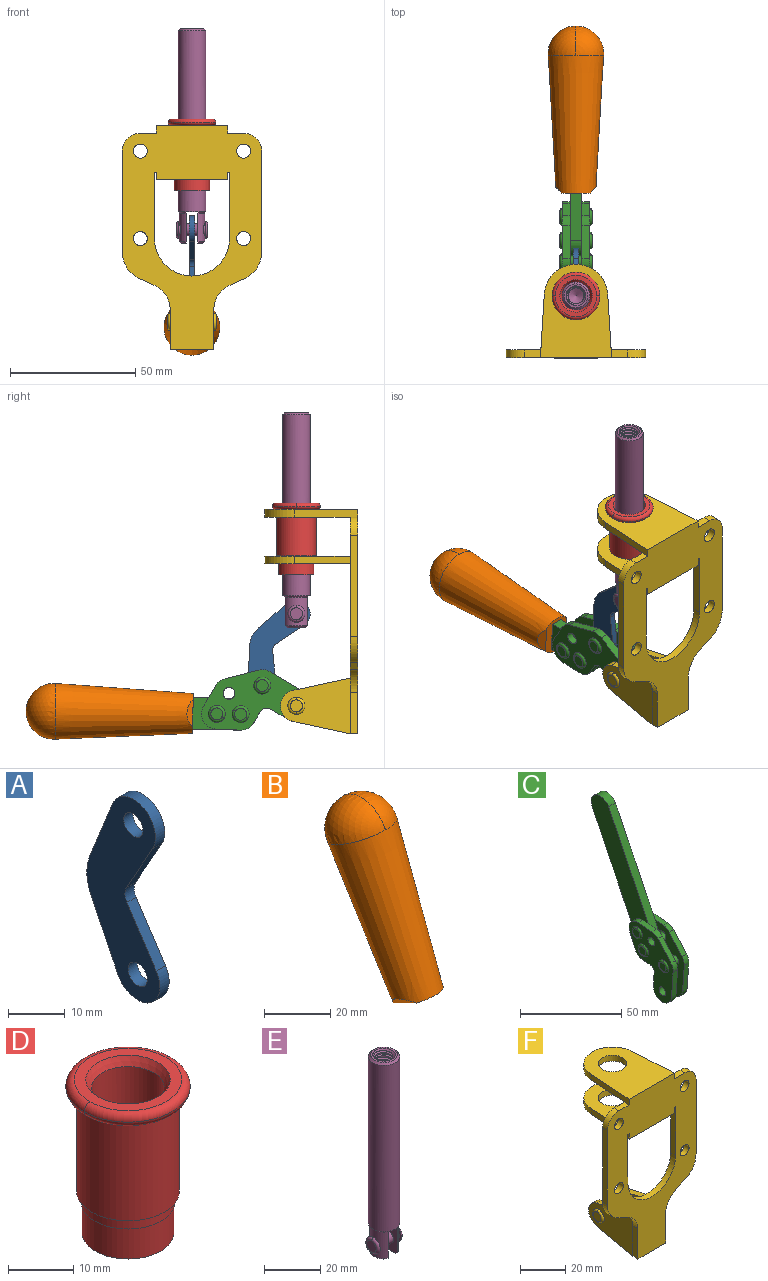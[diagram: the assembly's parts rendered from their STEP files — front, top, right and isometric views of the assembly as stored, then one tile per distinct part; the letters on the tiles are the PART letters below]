
ASSEMBLY  parts=6 mates=6
PART A: 12 faces, bbox 2.3x18.2x42.8 mm
  f0: cylinder r=2.4mm len=4.8mm, axis (1,0,0), area 34.9mm2, adj f4,f11
  f1: cylinder r=10.41mm len=8.47mm, axis (1,0,0), area 20.2mm2, adj f4,f9,f10,f11
  f2: cylinder r=3.05mm len=3.16mm, axis (1,0,0), area 7.7mm2, adj f4,f6,f7,f11
  f3: cylinder r=2.4mm len=4.8mm, axis (1,0,0), area 34.9mm2, adj f4,f11
  f4: plane 42.81x18.23mm, normal (-1,0,0), area 414.1mm2, adj f0,f1,f2,f3,f5,f6,f7,f8
  f5: cylinder r=5.54mm len=10.67mm, axis (1,0,0), area 41.8mm2, adj f4,f6,f10,f11
  f6: plane 11.66x6.53mm, normal (0,-0.87,-0.49), area 30.9mm2, adj f2,f4,f5,f11
  f7: plane 11.17x7.33mm, normal (0,-0.84,0.55), area 30.9mm2, adj f2,f4,f8,f11
  f8: cylinder r=5.54mm len=10.51mm, axis (1,0,0), area 41.8mm2, adj f4,f7,f9,f11
  f9: plane 13.67x6.67mm, normal (0,0.9,-0.44), area 35.1mm2, adj f1,f4,f8,f11
  f10: plane 14.1x5.7mm, normal (0,0.93,0.37), area 35.1mm2, adj f1,f4,f5,f11
  f11: plane 42.81x18.23mm, normal (1,0,0), area 414.1mm2, adj f0,f1,f2,f3,f5,f6,f7,f8
PART B: 11 faces, bbox 22.3x42.6x64.5 mm
  f0: sphere r=11.13mm, area 411.4mm2, adj f1,f8
  f1: cone r=11.11mm half-angle=3.3deg, axis (0,0.44,0.9), area 3251.8mm2, adj f0,f7,f8,f9,f10
  f2: cylinder r=6.16mm len=11.7mm, axis (1,0,0), area 89.5mm2, adj f3,f4,f5,f6
  f3: plane 60.23x36.75mm, normal (-1,0,0), area 763.6mm2, adj f2,f4,f6,f10
  f4: plane 51.37x25.05mm, normal (0,0.9,-0.44), area 264.2mm2, adj f2,f3,f5,f10
  f5: plane 60.23x36.75mm, normal (1,0,0), area 763.6mm2, adj f2,f4,f6,f10
  f6: plane 51.37x25.05mm, normal (0,-0.9,0.44), area 264.2mm2, adj f2,f3,f5,f10
  f7: plane 9.95x5.95mm, normal (0.71,-0.31,-0.64), area 25.8mm2, adj f1,f10
  f8: sphere r=11.13mm, area 411.4mm2, adj f0,f1
  f9: plane 9.95x5.95mm, normal (-0.71,-0.31,-0.64), area 25.8mm2, adj f1,f10
  f10: plane 14.27x11.38mm, normal (0,-0.44,-0.9), area 106.7mm2, adj f1,f3,f4,f5,f6,f7,f9
PART C: 59 faces, bbox 12.9x60.2x99.6 mm
  f0: torus R=2.39mm, axis (-1,0,0), area 14.9mm2, adj f20,f43,f51
  f1: torus R=2.39mm, axis (-1,0,0), area 14.9mm2, adj f19,f42,f51
  f2: torus R=2.39mm, axis (-1,0,0), area 14.9mm2, adj f18,f35,f51
  f3: torus R=2.39mm, axis (-1,0,0), area 14.9mm2, adj f14,f17,f23
  f4: torus R=2.39mm, axis (-1,0,0), area 14.9mm2, adj f13,f16,f23
  f5: torus R=2.39mm, axis (-1,0,0), area 14.9mm2, adj f12,f15,f23
  f6: cylinder r=2.39mm len=4.78mm, axis (1,0,0), area 46.5mm2, adj f48,f50,f51
  f7: cylinder r=2.39mm len=4.78mm, axis (1,0,0), area 46.5mm2, adj f50,f51
  f8: cylinder r=6.35mm len=12.68mm, axis (1,0,0), area 61.8mm2, adj f38,f39,f50,f51
  f9: cylinder r=2.39mm len=4.78mm, axis (-1,0,0), area 70.5mm2, adj f46,f50
  f10: cylinder r=2.39mm len=4.78mm, axis (-1,0,0), area 46.5mm2, adj f23,f45,f46
  f11: cylinder r=2.39mm len=4.78mm, axis (-1,0,0), area 46.5mm2, adj f23,f46
  f12: plane 4.78x4.78mm, normal (1,0,0), area 17.9mm2, adj f5,f15
  f13: plane 4.78x4.78mm, normal (1,0,0), area 17.9mm2, adj f4,f16
  f14: plane 4.78x4.78mm, normal (1,0,0), area 17.9mm2, adj f3,f17
  f15: torus R=2.39mm, axis (-1,0,0), area 14.9mm2, adj f5,f12,f23
  f16: torus R=2.39mm, axis (-1,0,0), area 14.9mm2, adj f4,f13,f23
  f17: torus R=2.39mm, axis (-1,0,0), area 14.9mm2, adj f3,f14,f23
  f18: plane 4.78x4.78mm, normal (-1,0,0), area 17.9mm2, adj f2,f35
  f19: plane 4.78x4.78mm, normal (-1,0,0), area 17.9mm2, adj f1,f42
  f20: plane 4.78x4.78mm, normal (-1,0,0), area 17.9mm2, adj f0,f43
  f21: plane 2.26x0.2mm, normal (1,0,0), area 0.2mm2, adj f31,f44
  f22: plane 2.26x0.2mm, normal (-1,0,0), area 0.2mm2, adj f41,f44
  f23: plane 39.37x30.77mm, normal (1,0,0), area 565.5mm2, adj f3,f4,f5,f10,f11,f15,f16,f17
  f24: cylinder r=6.1mm len=4.15mm, axis (-1,0,0), area 14.7mm2, adj f23,f25,f32,f46
  f25: plane 10.25x9.01mm, normal (0,-0.75,0.66), area 42.3mm2, adj f23,f24,f26,f46
  f26: cylinder r=6.35mm len=4.64mm, axis (-1,0,0), area 15.6mm2, adj f23,f25,f27,f46
  f27: plane 15.84x3.1mm, normal (0,-1,-0.07), area 49.2mm2, adj f23,f26,f28,f46
  f28: cylinder r=6.35mm len=12.68mm, axis (-1,0,0), area 61.8mm2, adj f23,f27,f29,f46
  f29: plane 8.11x3.1mm, normal (0,1,0.07), area 25.2mm2, adj f23,f28,f30,f46
  f30: cylinder r=3.05mm len=3.25mm, axis (-1,0,0), area 14.8mm2, adj f23,f29,f31,f46
  f31: plane 5.99x3.1mm, normal (0,0.07,-1), area 18.6mm2, adj f21,f23,f30,f44,f46
  f32: plane 9.5x3.1mm, normal (0,-0.07,1), area 29.5mm2, adj f23,f24,f33,f46,f47
  f33: cylinder r=6.1mm len=8.63mm, axis (-1,0,0), area 39.1mm2, adj f23,f32,f34,f47
  f34: plane 8.65x3.96mm, normal (0,0.91,-0.42), area 29.5mm2, adj f23,f33,f44,f47
  f35: torus R=2.39mm, axis (-1,0,0), area 14.9mm2, adj f2,f18,f51
  f36: plane 10.25x9.01mm, normal (0,-0.75,0.66), area 42.3mm2, adj f37,f49,f50,f51
  f37: cylinder r=6.35mm len=4.64mm, axis (1,0,0), area 15.6mm2, adj f36,f38,f50,f51
  f38: plane 15.84x3.1mm, normal (0,-1,-0.07), area 49.2mm2, adj f8,f37,f50,f51
  f39: plane 8.11x3.1mm, normal (0,1,0.07), area 25.2mm2, adj f8,f40,f50,f51
  f40: cylinder r=3.05mm len=3.25mm, axis (1,0,0), area 14.8mm2, adj f39,f41,f50,f51
  f41: plane 5.99x3.1mm, normal (0,0.07,-1), area 18.6mm2, adj f22,f40,f44,f50,f51
  f42: torus R=2.39mm, axis (-1,0,0), area 14.9mm2, adj f1,f19,f51
  f43: torus R=2.39mm, axis (-1,0,0), area 14.9mm2, adj f0,f20,f51
  f44: cylinder r=6.35mm len=12.12mm, axis (-1,0,0), area 128.9mm2, adj f21,f22,f23,f31,f34,f41,f46,f47
  f45: plane 2.65x1.35mm, normal (1,0,0), area 1mm2, adj f10,f55
  f46: plane 39.08x20.42mm, normal (-1,0,0), area 412.5mm2, adj f9,f10,f11,f24,f25,f26,f27,f28
  f47: plane 77.62x39.82mm, normal (1,0,0), area 850mm2, adj f32,f33,f34,f44,f53,f54,f55
  f48: plane 2.65x1.35mm, normal (-1,0,0), area 1mm2, adj f6,f55
  f49: cylinder r=6.1mm len=4.15mm, axis (1,0,0), area 14.7mm2, adj f36,f50,f51,f56
  f50: plane 39.08x20.42mm, normal (1,0,0), area 412.5mm2, adj f6,f7,f8,f9,f36,f37,f38,f39
  f51: plane 39.37x30.77mm, normal (-1,0,0), area 565.5mm2, adj f0,f1,f2,f6,f7,f8,f35,f36
  f52: plane 8.65x3.96mm, normal (0,0.91,-0.42), area 29.5mm2, adj f44,f51,f57,f58
  f53: plane 68.49x33.4mm, normal (0,0.9,-0.44), area 358.1mm2, adj f44,f47,f54,f58
  f54: cylinder r=6.35mm len=12.06mm, axis (1,0,0), area 93.7mm2, adj f47,f53,f55,f58
  f55: plane 68.49x33.4mm, normal (0,-0.9,0.44), area 358.1mm2, adj f44,f45,f46,f47,f48,f50,f54,f58
  f56: plane 9.5x3.1mm, normal (0,-0.07,1), area 29.5mm2, adj f49,f50,f51,f57,f58
  f57: cylinder r=6.1mm len=8.63mm, axis (1,0,0), area 39.1mm2, adj f51,f52,f56,f58
  f58: plane 77.62x39.82mm, normal (-1,0,0), area 850mm2, adj f44,f52,f53,f54,f55,f56,f57
PART D: 15 faces, bbox 20.6x20.6x28.7 mm
  f0: torus R=8.26mm, axis (0,0,1), area 56.8mm2, adj f1,f10,f12
  f1: torus R=8.26mm, axis (0,0,1), area 56.8mm2, adj f0,f6,f13
  f2: cylinder r=5.59mm len=25.91mm, axis (0,0,1), area 909.6mm2, adj f3,f4
  f3: cone r=6.86mm half-angle=45deg, axis (0,0,-1), area 70.2mm2, adj f2,f14
  f4: cone r=6.47mm half-angle=30deg, axis (0,0,1), area 66.7mm2, adj f2,f13
  f5: cylinder r=7.04mm len=14.07mm, axis (0,0,1), area 252.6mm2, adj f11,f14
  f6: torus R=8.26mm, axis (0,0,1), area 56.8mm2, adj f1,f12,f13
  f7: cylinder r=7.16mm len=14.33mm, axis (0,0,1), area 91.5mm2, adj f9,f11
  f8: cylinder r=7.86mm len=18.42mm, axis (0,0,1), area 909.6mm2, adj f9,f10
  f9: plane 15.72x15.72mm, normal (0,0,-1), area 33mm2, adj f7,f8
  f10: plane 16.51x16.51mm, normal (0,0,-1), area 19.9mm2, adj f0,f8,f12
  f11: plane 14.33x14.33mm, normal (0,0,-1), area 5.7mm2, adj f5,f7
  f12: torus R=8.26mm, axis (0,0,1), area 56.8mm2, adj f0,f6,f10
  f13: plane 16.51x16.51mm, normal (0,0,1), area 82.7mm2, adj f1,f4,f6
  f14: plane 14.07x14.07mm, normal (0,0,-1), area 7.8mm2, adj f3,f5
PART E: 48 faces, bbox 12.6x11.1x86.1 mm
  f0: torus R=2.41mm, axis (-1,0,0), area 15mm2, adj f30,f32,f34
  f1: torus R=2.41mm, axis (-1,0,0), area 15mm2, adj f29,f31,f33
  f2: cylinder r=5.54mm len=72.39mm, axis (0,0,1), area 2518.5mm2, adj f3,f4,f42,f43
  f3: cone r=5.54mm half-angle=45deg, axis (0,0,1), area 7.6mm2, adj f2,f5,f41
  f4: cone r=5.54mm half-angle=45deg, axis (0,0,-1), area 34.9mm2, adj f2,f39
  f5: cylinder r=5.08mm len=11.48mm, axis (0,0,1), area 108.3mm2, adj f3,f7,f8,f41
  f6: cylinder r=2.41mm len=4.83mm, axis (-1,0,0), area 71.2mm2, adj f40,f41
  f7: cylinder r=2.41mm len=4.83mm, axis (-1,0,0), area 7.6mm2, adj f5,f34
  f8: cone r=5.08mm half-angle=45deg, axis (0,0,1), area 10.6mm2, adj f5,f37,f41
  f9: cone r=3.98mm half-angle=45deg, axis (0,0,1), area 17.6mm2, adj f27,f39,f45,f46,f47
  f10: cylinder r=2.41mm len=4.83mm, axis (-1,0,0), area 7.6mm2, adj f33,f38
  f11: cylinder r=3.2mm len=6.4mm, axis (0,0,1), area 78.4mm2, adj f12,f28,f44,f45,f47
  f12: cylinder r=3.2mm len=6.4mm, axis (0,0,1), area 10.5mm2, adj f11,f13,f45,f47
  f13: cylinder r=3.2mm len=6.4mm, axis (0,0,1), area 10.5mm2, adj f12,f14,f45,f47
  f14: cylinder r=3.2mm len=6.4mm, axis (0,0,1), area 10.5mm2, adj f13,f15,f45,f47
  f15: cylinder r=3.2mm len=6.4mm, axis (0,0,1), area 10.5mm2, adj f14,f16,f45,f47
  f16: cylinder r=3.2mm len=6.4mm, axis (0,0,1), area 10.5mm2, adj f15,f17,f45,f47
  f17: cylinder r=3.2mm len=6.4mm, axis (0,0,1), area 10.5mm2, adj f16,f18,f45,f47
  f18: cylinder r=3.2mm len=6.4mm, axis (0,0,1), area 10.5mm2, adj f17,f19,f45,f47
  f19: cylinder r=3.2mm len=6.4mm, axis (0,0,1), area 10.5mm2, adj f18,f20,f45,f47
  f20: cylinder r=3.2mm len=6.4mm, axis (0,0,1), area 10.5mm2, adj f19,f21,f45,f47
  f21: cylinder r=3.2mm len=6.4mm, axis (0,0,1), area 10.5mm2, adj f20,f22,f45,f47
  f22: cylinder r=3.2mm len=6.4mm, axis (0,0,1), area 10.5mm2, adj f21,f23,f45,f47
  f23: cylinder r=3.2mm len=6.4mm, axis (0,0,1), area 10.5mm2, adj f22,f24,f45,f47
  f24: cylinder r=3.2mm len=6.4mm, axis (0,0,1), area 10.5mm2, adj f23,f25,f45,f47
  f25: cylinder r=3.2mm len=6.4mm, axis (0,0,1), area 10.5mm2, adj f24,f26,f45,f47
  f26: cylinder r=3.2mm len=6.4mm, axis (0,0,1), area 10.5mm2, adj f25,f27,f45,f47
  f27: cylinder r=3.2mm len=6.4mm, axis (0,0,1), area 7.4mm2, adj f9,f26,f45,f47
  f28: cone r=3.2mm half-angle=60deg, axis (0,0,1), area 37.2mm2, adj f11
  f29: plane 4.83x4.83mm, normal (-1,0,0), area 18.3mm2, adj f1,f31
  f30: plane 4.83x4.83mm, normal (1,0,0), area 18.3mm2, adj f0,f32
  f31: torus R=2.41mm, axis (-1,0,0), area 15mm2, adj f1,f29,f33
  f32: torus R=2.41mm, axis (-1,0,0), area 15mm2, adj f0,f30,f34
  f33: plane 6.83x6.83mm, normal (1,0,0), area 18.3mm2, adj f1,f10,f31
  f34: plane 6.83x6.83mm, normal (-1,0,0), area 18.3mm2, adj f0,f7,f32
  f35: cone r=5.08mm half-angle=45deg, axis (0,0,1), area 10.6mm2, adj f36,f38,f40
  f36: plane 7.25x1.97mm, normal (0,0,-1), area 10mm2, adj f35,f40
  f37: plane 7.25x1.97mm, normal (0,0,-1), area 10mm2, adj f8,f41
  f38: cylinder r=5.08mm len=11.48mm, axis (0,0,1), area 108.3mm2, adj f10,f35,f40,f42
  f39: plane 9.55x9.55mm, normal (0,0,1), area 22mm2, adj f4,f9
  f40: plane 12.76x10.09mm, normal (1,0,0), area 95.7mm2, adj f6,f35,f36,f38,f42,f43
  f41: plane 12.76x10.09mm, normal (-1,0,0), area 95.7mm2, adj f3,f5,f6,f8,f37,f43
  f42: cone r=5.54mm half-angle=45deg, axis (0,0,1), area 7.6mm2, adj f2,f38,f40
  f43: plane 11.07x4.7mm, normal (0,0,-1), area 50.4mm2, adj f2,f40,f41
  f44: plane 0.89x0.62mm, normal (-1,0,0), area 0.3mm2, adj f11,f45,f46,f47
  f45: bspline ~24.8x7.63mm, area 266.6mm2, adj f9,f11,f12,f13,f14,f15,f16,f17
  f46: bspline ~24.87x7.63mm, area 73.6mm2, adj f9,f44,f45,f47
  f47: bspline ~24.98x7.63mm, area 272.5mm2, adj f9,f11,f12,f13,f14,f15,f16,f17
PART F: 55 faces, bbox 55.7x37.4x89.8 mm
  f0: torus R=2.41mm, axis (-1,0,0), area 15mm2, adj f11,f15,f25
  f1: torus R=2.41mm, axis (-1,0,0), area 15mm2, adj f10,f12,f22
  f2: cylinder r=2.78mm len=5.56mm, axis (0,-1,0), area 54.2mm2, adj f30,f54
  f3: cylinder r=14.99mm len=29.97mm, axis (0,-1,0), area 145.9mm2, adj f30,f49,f53,f54
  f4: cylinder r=2.78mm len=5.56mm, axis (0,-1,0), area 54.2mm2, adj f30,f54
  f5: cylinder r=2.78mm len=5.56mm, axis (0,-1,0), area 54.2mm2, adj f30,f54
  f6: cylinder r=2.78mm len=5.56mm, axis (0,-1,0), area 54.2mm2, adj f30,f54
  f7: cylinder r=6.35mm len=12.7mm, axis (0,0,1), area 123.6mm2, adj f27,f51
  f8: cylinder r=6.35mm len=12.7mm, axis (0,0,-1), area 124.7mm2, adj f21,f35
  f9: cylinder r=2.41mm len=11.18mm, axis (-1,0,0), area 169.4mm2, adj f16,f19
  f10: plane 4.83x4.83mm, normal (1,0,0), area 18.3mm2, adj f1,f12
  f11: plane 4.83x4.83mm, normal (-1,0,0), area 18.3mm2, adj f0,f15
  f12: torus R=2.41mm, axis (-1,0,0), area 15mm2, adj f1,f10,f22
  f13: cylinder r=6.35mm len=12.41mm, axis (1,0,0), area 53.4mm2, adj f18,f19,f22,f23
  f14: cylinder r=6.35mm len=12.41mm, axis (-1,0,0), area 53.4mm2, adj f16,f17,f24,f25
  f15: torus R=2.41mm, axis (-1,0,0), area 15mm2, adj f0,f11,f25
  f16: plane 27.86x22.35mm, normal (1,0,0), area 425.4mm2, adj f9,f14,f17,f24,f30
  f17: plane 22.86x4.97mm, normal (0,0.21,0.98), area 72.5mm2, adj f14,f16,f25,f30
  f18: plane 22.86x4.97mm, normal (0,0.21,0.98), area 72.5mm2, adj f13,f19,f22,f30
  f19: plane 27.86x22.35mm, normal (-1,0,0), area 425.4mm2, adj f9,f13,f18,f23,f30
  f20: cylinder r=12.7mm len=25.35mm, axis (0,0,-1), area 119.8mm2, adj f21,f34,f35,f36
  f21: plane 34.21x28.07mm, normal (0,0,-1), area 702.4mm2, adj f8,f20,f30,f34,f36
  f22: plane 27.96x22.45mm, normal (1,0,0), area 407.2mm2, adj f1,f12,f13,f18,f23,f30,f42,f43
  f23: plane 22.86x4.97mm, normal (0,0.21,-0.98), area 72.5mm2, adj f13,f19,f22,f44
  f24: plane 22.86x4.97mm, normal (0,0.21,-0.98), area 72.5mm2, adj f14,f16,f25,f44
  f25: plane 27.86x22.35mm, normal (-1,0,0), area 407.1mm2, adj f0,f14,f15,f17,f24,f30,f45,f46
  f26: plane 3.1x0.95mm, normal (0,0,-1), area 2.7mm2, adj f30,f49,f50,f54
  f27: plane 34.21x28.07mm, normal (0,0,1), area 702.4mm2, adj f7,f28,f30,f50,f52
  f28: cylinder r=12.7mm len=25.35mm, axis (0,0,1), area 118.8mm2, adj f27,f50,f51,f52
  f29: plane 3.1x0.95mm, normal (0,0,-1), area 2.7mm2, adj f30,f52,f53,f54
  f30: plane 86.54x55.63mm, normal (0,1,0), area 2362.9mm2, adj f2,f3,f4,f5,f6,f16,f17,f18
  f31: plane 40.56x3.1mm, normal (-1,0,0), area 125.7mm2, adj f30,f32,f48,f54
  f32: cylinder r=7.11mm len=7.11mm, axis (0,-1,0), area 34.6mm2, adj f30,f31,f33,f54
  f33: plane 6.67x3.1mm, normal (0,0,1), area 20.4mm2, adj f30,f32,f34,f54
  f34: plane 25.39x3.13mm, normal (-1,0.06,0), area 79.5mm2, adj f20,f21,f33,f35,f54
  f35: plane 37.31x28.45mm, normal (0,0,1), area 789.9mm2, adj f8,f20,f34,f36,f54
  f36: plane 25.39x3.13mm, normal (1,0.06,0), area 79.5mm2, adj f20,f21,f35,f37,f54
  f37: plane 6.67x3.1mm, normal (0,0,1), area 20.4mm2, adj f30,f36,f38,f54
  f38: cylinder r=7.11mm len=7.11mm, axis (0,-1,0), area 34.6mm2, adj f30,f37,f39,f54
  f39: plane 40.56x3.1mm, normal (1,0,0), area 125.7mm2, adj f30,f38,f40,f54
  f40: cylinder r=11.18mm len=10.16mm, axis (0,-1,0), area 39.5mm2, adj f30,f39,f41,f54
  f41: plane 6.09x3.1mm, normal (0.42,0,-0.91), area 20.8mm2, adj f30,f40,f42,f54
  f42: cylinder r=11.18mm len=9.41mm, axis (0,-1,0), area 37.2mm2, adj f22,f30,f41,f43,f54
  f43: plane 16.5x3.1mm, normal (1,0,0), area 51.1mm2, adj f22,f42,f44,f54
  f44: plane 17.37x3.1mm, normal (0,0,-1), area 53.8mm2, adj f23,f24,f30,f43,f45,f54
  f45: plane 16.5x3.1mm, normal (-1,0,0), area 51.1mm2, adj f25,f44,f46,f54
  f46: cylinder r=11.18mm len=9.41mm, axis (0,-1,0), area 37.2mm2, adj f25,f30,f45,f47,f54
  f47: plane 6.09x3.1mm, normal (-0.42,0,-0.91), area 20.8mm2, adj f30,f46,f48,f54
  f48: cylinder r=11.18mm len=10.16mm, axis (0,-1,0), area 39.5mm2, adj f30,f31,f47,f54
  f49: plane 26.54x3.1mm, normal (-1,0,0), area 82.3mm2, adj f3,f26,f30,f54
  f50: plane 25.39x3.1mm, normal (1,0.06,0), area 78.8mm2, adj f26,f27,f28,f51,f54
  f51: plane 37.31x28.45mm, normal (0,0,-1), area 789.9mm2, adj f7,f28,f50,f52,f54
  f52: plane 25.39x3.1mm, normal (-1,0.06,0), area 78.8mm2, adj f27,f28,f29,f51,f54
  f53: plane 26.54x3.1mm, normal (1,0,0), area 82.3mm2, adj f3,f29,f30,f54
  f54: plane 89.66x55.63mm, normal (0,-1,0), area 2678.5mm2, adj f2,f3,f4,f5,f6,f26,f29,f31
PLACE A rot(axis=(1,0,0),27.4deg) t=(0,9.89,-20.33)mm
PLACE B rot(axis=(-1,0,0),63.1deg) t=(-0.04,42.11,4.37)mm
PLACE C rot(axis=(-1,0,0),63.1deg) t=(0,42.11,4.37)mm
PLACE D at identity
PLACE E t=(0,0,-10.74)mm
PLACE F at identity fixed
MATE revolute A.f3 <-> C.f4  axis (1,0,0) through (0,38.24,-23.94)mm
MATE revolute A.f5 <-> E.f6  axis (1,0,0) through (0,24.61,4.74)mm
MATE revolute C.f7 <-> F.f0  axis (-1,0,0) through (0,24.61,-32.09)mm
MATE slider E.f2 <-> D.f0  axis (0,0,1) through (0,24.61,48.04)mm
MATE fastened D.f2 <-> F.f7  axis (0,0,1) through (0,24.61,46.39)mm
MATE fastened B.f2 <-> C.f54  axis (1,0,0) through (-2.35,123.08,-34.22)mm
